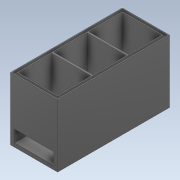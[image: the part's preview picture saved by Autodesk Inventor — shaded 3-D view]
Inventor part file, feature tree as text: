
AUTODESK INVENTOR PART (.ipt)
format: ipt  version: 2020 (Build 240168000, 168)  size: 153,600 bytes
history: native  units: mm
features: sketch x6, extrude x4
ambient origin geometry x8: Origin, YZ Plane, XZ Plane, XY Plane, X Axis, Y Axis, Z Axis, Center Point
bodies: Volumenkörper1 (feature_tree)
feature tree (10):
  extrude  "Extrusion1"  Depth=160.0mm
  sketch  "Skizze2"  dims[d2=285.0mm d3=0.0mm d4=10.0mm]
  extrude  "Extrusion2"  Depth=10.0mm
  sketch  "Skizze4"  dims[d7=30.0mm d8=275.0mm d9=0.0mm]
  extrude  "Extrusion3"  Depth=10.0mm
  extrude  "Extrusion4"  Depth=275.0mm TaperAngle=0.0deg
  sketch  "Skizze1"  dims[d0=120.0mm d1=160.0mm]
  sketch  "Skizze3"  dims[d5=10.0mm d6=10.0mm]
  sketch  "Skizze5"  dims[d10=10.0mm]
  sketch  "Skizze6"  dims[d11=10.0mm d12=5.0mm d13=85.0mm d14=85.0mm d15=5.0mm d16=85.0mm d17=10.0mm d18=10.0mm d19=110.0mm d20=0.0mm d21=2.5mm d22=2.5mm d23=2.5mm d24=2.5mm d25=2.5mm d26=2.5mm d27=2.5mm d28=2.5mm d29=5.0mm d30=0.0mm]
